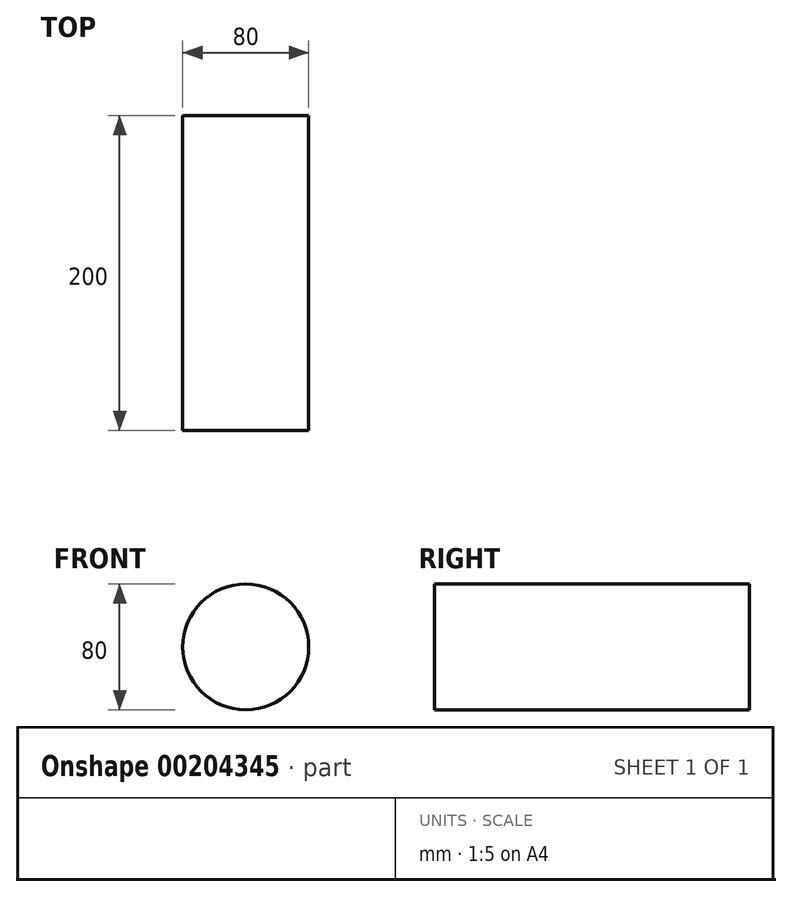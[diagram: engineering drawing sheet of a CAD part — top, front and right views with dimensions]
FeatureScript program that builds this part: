
annotation { "Feature Type Name" : "Feature", "Feature Type Description" : "" }
export const myFeature = defineFeature(function(context is Context, id is Id, definition is map)
    precondition{}
    {
        {
            var Q0;
            Q0=qCreatedBy(makeId("Front.planeOp"),FACE);
            var sketch = newSketch(context, id + "F0", { "sketchPlane" : qUnion([Q0])});
            skCircle(sketch, "E0", {"center": v(0, 0) * mm, "radius": 40 * mm});
            skSolve(sketch);
        }
        {
            var Q0;
            Q0 = qSketchRegion(id + "F0", true);
            extrude(context, id + "F1", {"entities" : qUnion([Q0]), "depth" : 200 * mm});
        }
    });
